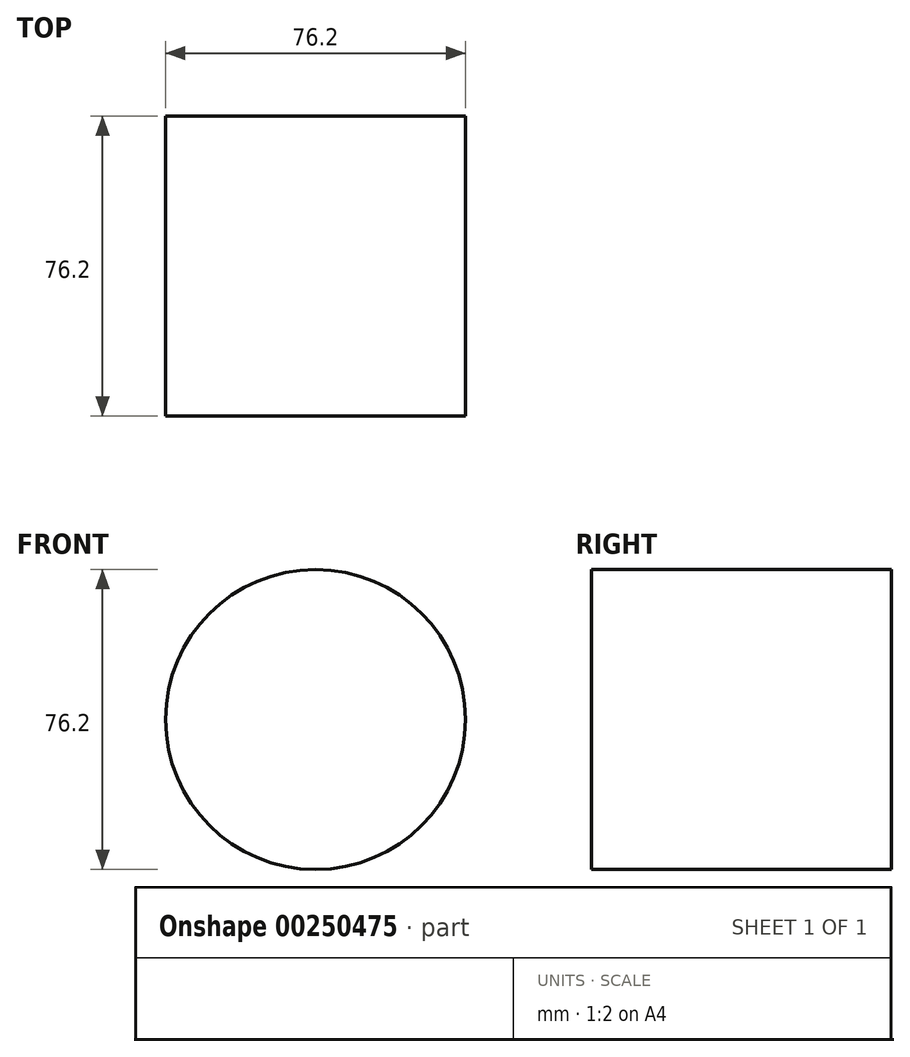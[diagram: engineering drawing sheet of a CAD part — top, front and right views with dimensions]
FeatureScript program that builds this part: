
annotation { "Feature Type Name" : "Feature", "Feature Type Description" : "" }
export const myFeature = defineFeature(function(context is Context, id is Id, definition is map)
    precondition{}
    {
        {
            var Q0;
            Q0=qCreatedBy(makeId("Front.planeOp"),FACE);
            var sketch = newSketch(context, id + "F0", { "sketchPlane" : qUnion([Q0])});
            skCircle(sketch, "E0", {"center": v(0, 0) * mm, "radius": 38.1 * mm});
            skSolve(sketch);
        }
        {
            var Q0;
            Q0=makeQuery(id+"F0.imprint","IMPRINT",FACE,{"disambiguationData":[TD([[makeQuery(id+"F0.imprint","IMPRINT",EDGE,{"derivedFrom":sQuery(id+"F0.wireOp",EDGE,"E0")}),1.0]])]});
            extrude(context, id + "F1", {"entities" : qUnion([Q0]), "oppositeDirection" : true, "depth" : 38.1 * mm});
        }
        {
            var Q0;
            Q0=makeQuery(id+"F1.opExtrude","CAP_FACE",FACE,{"disambiguationData":[OSD([sQuery(id+"F0.wireOp",EDGE,"E0")])],"isStart":false});
            extrude(context, id + "F2", {"entities" : qUnion([Q0]), "operationType" : NewBodyOperationType.ADD, "depth" : 38.1 * mm});
        }
    });
